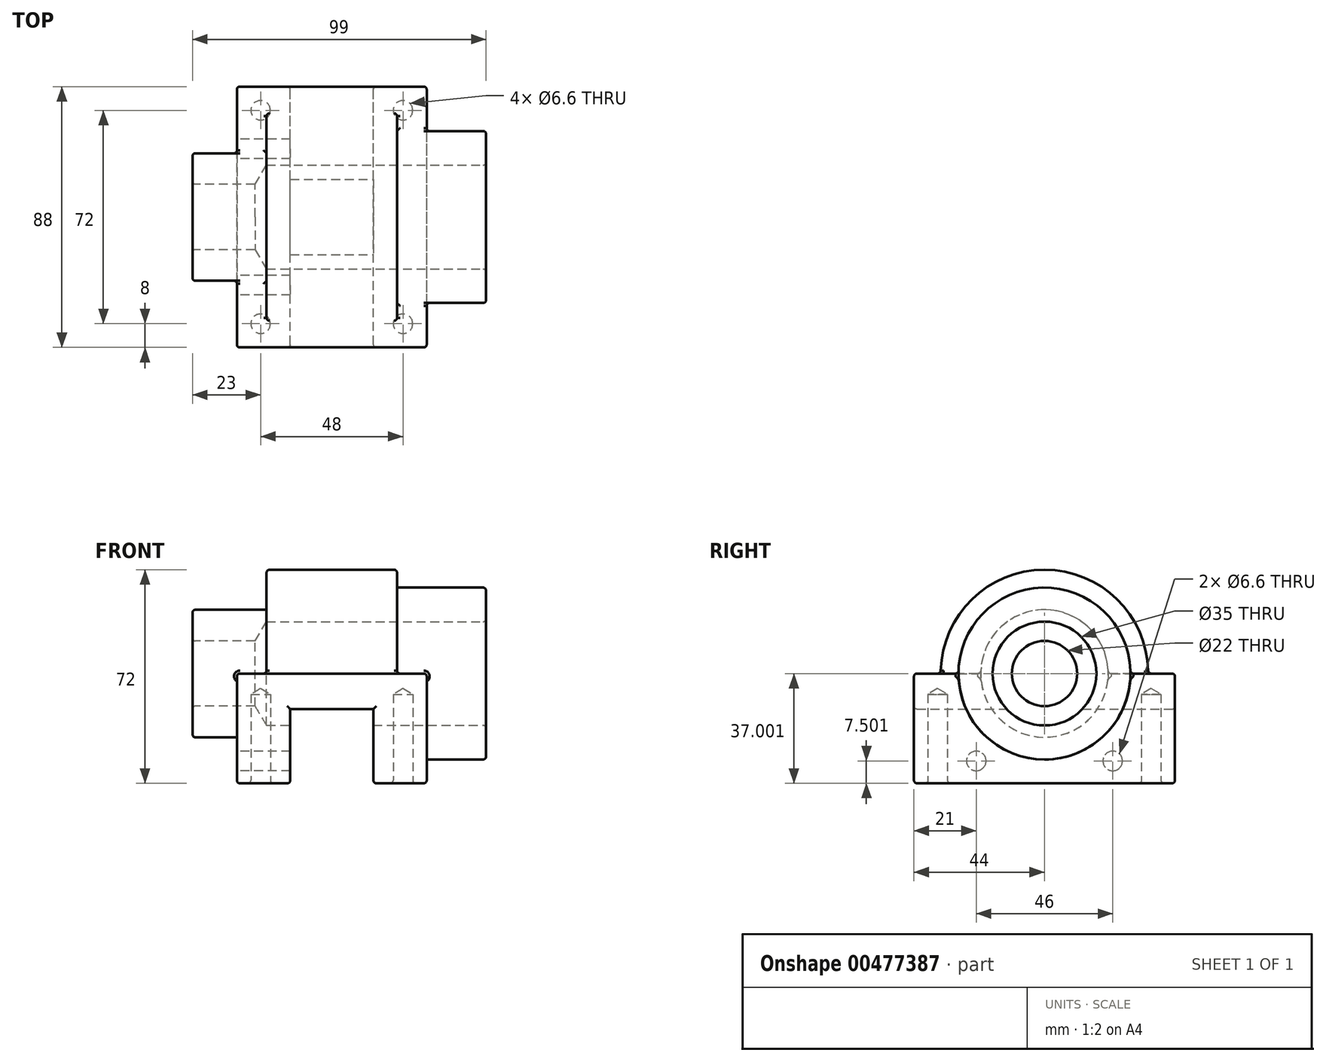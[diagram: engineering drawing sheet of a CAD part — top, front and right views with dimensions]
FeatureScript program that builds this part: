
annotation { "Feature Type Name" : "Feature", "Feature Type Description" : "" }
export const myFeature = defineFeature(function(context is Context, id is Id, definition is map)
    precondition{}
    {
        {
            var Q0;
            Q0=qCreatedBy(makeId("Front.planeOp"),FACE);
            var sketch = newSketch(context, id + "F0", { "sketchPlane" : qUnion([Q0])});
            skLineSegment(sketch, "E0", {"start": v(-32, -20.13) * mm, "end": v(-32, 16.87) * mm});
            skLineSegment(sketch, "E1", {"start": v(-32, 16.87) * mm, "end": v(32, 16.87) * mm});
            skLineSegment(sketch, "E2", {"start": v(32, 16.87) * mm, "end": v(32, -20.13) * mm});
            skLineSegment(sketch, "E3", {"start": v(32, -20.13) * mm, "end": v(14, -20.13) * mm});
            skLineSegment(sketch, "E4", {"start": v(14, -20.13) * mm, "end": v(14, 4.87) * mm});
            skLineSegment(sketch, "E5", {"start": v(14, 4.87) * mm, "end": v(-14, 4.87) * mm});
            skLineSegment(sketch, "E6", {"start": v(-14, 4.87) * mm, "end": v(-14, -20.13) * mm});
            skLineSegment(sketch, "E7", {"start": v(-14, -20.13) * mm, "end": v(-32, -20.13) * mm});
            skSolve(sketch);
        }
        {
            var Q0;
            Q0=makeQuery(id+"F0.imprint","IMPRINT",FACE,{"disambiguationData":[TD([[makeQuery(id+"F0.imprint","IMPRINT",EDGE,{"derivedFrom":sQuery(id+"F0.wireOp",EDGE,"E0")}),-1.0]])]});
            extrude(context, id + "F1", {"entities" : qUnion([Q0]), "depth" : 88 * mm});
        }
        {
            var Q0;
            Q0=makeQuery(id+"F1.opExtrude","SWEPT_FACE",FACE,{"disambiguationData":[OSD([sQuery(id+"F0.wireOp",EDGE,"E2")])]});
            var sketch = newSketch(context, id + "F2", { "sketchPlane" : qUnion([Q0])});
            skCircle(sketch, "E8", {"center": v(-44, 16.87) * mm, "radius": 29 * mm});
            skSolve(sketch);
        }
        {
            var Q0;
            {var subQ0=sQuery(id+"F2.wireOp",EDGE,"E8");var subQ1=makeQuery(id+"F1.opExtrude","SWEPT_EDGE",EDGE,{"disambiguationData":[OSD([sQuery(id+"F0.wireOp",EDGE,"E1"),sQuery(id+"F0.wireOp",EDGE,"E2")])]});var subQ2=makeQuery(id+"F2.imprint","INTERSECT",VERTEX,{"disambiguationData":[OD(0.0)],"derivedFrom":[subQ1,subQ0]});Q0=makeQuery(id+"F2.imprint","IMPRINT",FACE,{"disambiguationData":[TD([[makeQuery(id+"F2.imprint","IMPRINT",EDGE,{"disambiguationData":[TD([[subQ2,1.0]])],"derivedFrom":subQ0}),1.0]])]});}
            var Q1;
            {var subQ0=sQuery(id+"F2.wireOp",EDGE,"E8");var subQ1=makeQuery(id+"F1.opExtrude","SWEPT_EDGE",EDGE,{"disambiguationData":[OSD([sQuery(id+"F0.wireOp",EDGE,"E1"),sQuery(id+"F0.wireOp",EDGE,"E2")])]});var subQ2=makeQuery(id+"F2.imprint","INTERSECT",VERTEX,{"disambiguationData":[OD(0.0)],"derivedFrom":[subQ1,subQ0]});Q1=makeQuery(id+"F2.imprint","IMPRINT",FACE,{"disambiguationData":[TD([[makeQuery(id+"F2.imprint","IMPRINT",EDGE,{"disambiguationData":[TD([[subQ2,-1.0]])],"derivedFrom":subQ0}),1.0]])]});}
            extrude(context, id + "F3", {"entities" : qUnion([Q0, Q1]), "operationType" : NewBodyOperationType.ADD, "depth" : 20 * mm});
        }
        {
            var Q0;
            Q0=makeQuery(id+"F3.opExtrude","CAP_FACE",FACE,{"disambiguationData":[OSD([sQuery(id+"F2.wireOp",EDGE,"E8")])],"isStart":true});
            extrude(context, id + "F4", {"entities" : qUnion([Q0]), "operationType" : NewBodyOperationType.ADD, "depth" : 10 * mm});
        }
        {
            var Q0;
            Q0=makeQuery(id+"F1.opExtrude","SWEPT_FACE",FACE,{"disambiguationData":[OSD([sQuery(id+"F0.wireOp",EDGE,"E0")])]});
            var sketch = newSketch(context, id + "F5", { "sketchPlane" : qUnion([Q0])});
            skCircle(sketch, "E9", {"center": v(44, 16.87) * mm, "radius": 21.5 * mm});
            skSolve(sketch);
        }
        {
            var Q0;
            {var subQ0=sQuery(id+"F5.wireOp",EDGE,"E9");var subQ1=makeQuery(id+"F1.opExtrude","SWEPT_EDGE",EDGE,{"disambiguationData":[OSD([sQuery(id+"F0.wireOp",EDGE,"E0"),sQuery(id+"F0.wireOp",EDGE,"E1")])]});var subQ2=makeQuery(id+"F5.imprint","INTERSECT",VERTEX,{"disambiguationData":[OD(0.0)],"derivedFrom":[subQ1,subQ0]});Q0=makeQuery(id+"F5.imprint","IMPRINT",FACE,{"disambiguationData":[TD([[makeQuery(id+"F5.imprint","IMPRINT",EDGE,{"disambiguationData":[TD([[subQ2,1.0]])],"derivedFrom":subQ0}),1.0]])]});}
            var Q1;
            {var subQ0=sQuery(id+"F5.wireOp",EDGE,"E9");var subQ1=makeQuery(id+"F1.opExtrude","SWEPT_EDGE",EDGE,{"disambiguationData":[OSD([sQuery(id+"F0.wireOp",EDGE,"E0"),sQuery(id+"F0.wireOp",EDGE,"E1")])]});var subQ2=makeQuery(id+"F5.imprint","INTERSECT",VERTEX,{"disambiguationData":[OD(0.0)],"derivedFrom":[subQ1,subQ0]});Q1=makeQuery(id+"F5.imprint","IMPRINT",FACE,{"disambiguationData":[TD([[makeQuery(id+"F5.imprint","IMPRINT",EDGE,{"disambiguationData":[TD([[subQ2,-1.0]])],"derivedFrom":subQ0}),1.0]])]});}
            extrude(context, id + "F6", {"entities" : qUnion([Q0, Q1]), "operationType" : NewBodyOperationType.ADD, "depth" : 15 * mm});
        }
        {
            var Q0;
            Q0=makeQuery(id+"F6.opExtrude","CAP_FACE",FACE,{"disambiguationData":[OSD([sQuery(id+"F5.wireOp",EDGE,"E9")])],"isStart":true});
            extrude(context, id + "F7", {"entities" : qUnion([Q0]), "operationType" : NewBodyOperationType.ADD, "depth" : 10 * mm});
        }
        {
            var Q0;
            Q0=makeQuery(id+"F4.opExtrude","CAP_FACE",FACE,{"disambiguationData":[OSD([sQuery(id+"F2.wireOp",EDGE,"E8")])],"isStart":false});
            var sketch = newSketch(context, id + "F8", { "sketchPlane" : qUnion([Q0])});
            skArc(sketch, "E10", {"start": v(9, 16.87) * mm, "mid": v(44, 51.87) * mm, "end": v(79, 16.87) * mm});
            skLineSegment(sketch, "E11", {"start": v(9, 16.87) * mm, "end": v(79, 16.87) * mm});
            skSolve(sketch);
        }
        {
            var Q0;
            Q0 = qSketchRegion(id + "F8", true);
            extrude(context, id + "F9", {"entities" : qUnion([Q0]), "operationType" : NewBodyOperationType.ADD, "depth" : 44 * mm});
        }
        {
            var Q0;
            Q0=makeQuery(id+"F3.opExtrude","CAP_FACE",FACE,{"disambiguationData":[OSD([sQuery(id+"F2.wireOp",EDGE,"E8")])],"isStart":false});
            var sketch = newSketch(context, id + "F10", { "sketchPlane" : qUnion([Q0])});
            skPoint(sketch, "E12", {"position": v(-44, 16.87) * mm});
            skSolve(sketch);
        }
        {
            var Q0;
            Q0=sQuery(id+"F10.wireOp",VERTEX,"E12");
            var Q1;
            Q1=makeQuery(id+"F1.opExtrude","SWEPT_BODY",BODY,{"disambiguationData":[OSD([sQuery(id+"F0.wireOp",EDGE,"E0"),sQuery(id+"F0.wireOp",EDGE,"E1"),sQuery(id+"F0.wireOp",EDGE,"E2"),sQuery(id+"F0.wireOp",EDGE,"E3"),sQuery(id+"F0.wireOp",EDGE,"E4"),sQuery(id+"F0.wireOp",EDGE,"E5"),sQuery(id+"F0.wireOp",EDGE,"E6"),sQuery(id+"F0.wireOp",EDGE,"E7")])]});
            hole(context, id + "F11", {"style" : HoleStyle.SIMPLE, "endStyle" : HoleEndStyle.BLIND, "holeDiameter" : 35 * mm, "holeDepth" : 74 * mm, "isTappedThrough" : true, "tappedDepth" : 12 * mm, "tapClearance" : 3, "locations" : qUnion([Q0]), "scope" : qUnion([Q1])});
        }
        {
            var Q0;
            Q0=makeQuery(id+"F6.opExtrude","CAP_FACE",FACE,{"disambiguationData":[OSD([sQuery(id+"F5.wireOp",EDGE,"E9")])],"isStart":false});
            var sketch = newSketch(context, id + "F12", { "sketchPlane" : qUnion([Q0])});
            skPoint(sketch, "E13", {"position": v(44, 16.87) * mm});
            skSolve(sketch);
        }
        {
            var Q0;
            Q0=sQuery(id+"F12.wireOp",VERTEX,"E13");
            var Q1;
            Q1=makeQuery(id+"F1.opExtrude","SWEPT_BODY",BODY,{"disambiguationData":[OSD([sQuery(id+"F0.wireOp",EDGE,"E0"),sQuery(id+"F0.wireOp",EDGE,"E1"),sQuery(id+"F0.wireOp",EDGE,"E2"),sQuery(id+"F0.wireOp",EDGE,"E3"),sQuery(id+"F0.wireOp",EDGE,"E4"),sQuery(id+"F0.wireOp",EDGE,"E5"),sQuery(id+"F0.wireOp",EDGE,"E6"),sQuery(id+"F0.wireOp",EDGE,"E7")])]});
            hole(context, id + "F13", {"style" : HoleStyle.SIMPLE, "endStyle" : HoleEndStyle.BLIND, "holeDiameter" : 22 * mm, "holeDepth" : 25 * mm, "isTappedThrough" : true, "tappedDepth" : 12 * mm, "tapClearance" : 3, "locations" : qUnion([Q0]), "scope" : qUnion([Q1])});
        }
        {
            var Q0;
            Q0=makeQuery(id+"F1.opExtrude","SWEPT_FACE",FACE,{"disambiguationData":[OSD([sQuery(id+"F0.wireOp",EDGE,"E7")])]});
            var sketch = newSketch(context, id + "F14", { "sketchPlane" : qUnion([Q0])});
            skPoint(sketch, "E14", {"position": v(-24, 80) * mm});
            skPoint(sketch, "E15", {"position": v(-24, 8) * mm});
            skPoint(sketch, "E16.MirrorP", {"position": v(24, 8) * mm});
            skPoint(sketch, "E17.MirrorP", {"position": v(24, 80) * mm});
            skSolve(sketch);
        }
        {
            var Q0;
            Q0=sQuery(id+"F14.wireOp",VERTEX,"E14");
            var Q1;
            Q1=sQuery(id+"F14.wireOp",VERTEX,"E17.MirrorP");
            var Q2;
            Q2=sQuery(id+"F14.wireOp",VERTEX,"E15");
            var Q3;
            Q3=sQuery(id+"F14.wireOp",VERTEX,"E16.MirrorP");
            var Q4;
            Q4=makeQuery(id+"F1.opExtrude","SWEPT_BODY",BODY,{"disambiguationData":[OSD([sQuery(id+"F0.wireOp",EDGE,"E0"),sQuery(id+"F0.wireOp",EDGE,"E1"),sQuery(id+"F0.wireOp",EDGE,"E2"),sQuery(id+"F0.wireOp",EDGE,"E3"),sQuery(id+"F0.wireOp",EDGE,"E4"),sQuery(id+"F0.wireOp",EDGE,"E5"),sQuery(id+"F0.wireOp",EDGE,"E6"),sQuery(id+"F0.wireOp",EDGE,"E7")])]});
            hole(context, id + "F15", {"style" : HoleStyle.SIMPLE, "endStyle" : HoleEndStyle.BLIND, "standardTappedOrClearance" : lookupTablePath({ "standard" : "ISO", "fit" : "Normal", "size" : "M6", "type" : "Clearance" }), "standardBlindInLast" : lookupTablePath({ "fit" : "Standard", "standard" : "ISO", "size" : "M6", "type" : "Clearance" }), "holeDiameter" : 6.6 * mm, "holeDepth" : 30 * mm, "isTappedThrough" : true, "tappedDepth" : 12 * mm, "tapClearance" : 3, "locations" : qUnion([Q0, Q1, Q2, Q3]), "scope" : qUnion([Q4])});
        }
        {
            var Q0;
            Q0=makeQuery(id+"F1.opExtrude","SWEPT_FACE",FACE,{"disambiguationData":[OSD([sQuery(id+"F0.wireOp",EDGE,"E0")])]});
            var sketch = newSketch(context, id + "F16", { "sketchPlane" : qUnion([Q0])});
            skPoint(sketch, "E18", {"position": v(67, -12.63) * mm});
            skPoint(sketch, "E19", {"position": v(21, -12.63) * mm});
            skSolve(sketch);
        }
        {
            var Q0;
            Q0=sQuery(id+"F16.wireOp",VERTEX,"E18");
            var Q1;
            Q1=sQuery(id+"F16.wireOp",VERTEX,"E19");
            var Q2;
            Q2=makeQuery(id+"F1.opExtrude","SWEPT_BODY",BODY,{"disambiguationData":[OSD([sQuery(id+"F0.wireOp",EDGE,"E0"),sQuery(id+"F0.wireOp",EDGE,"E1"),sQuery(id+"F0.wireOp",EDGE,"E2"),sQuery(id+"F0.wireOp",EDGE,"E3"),sQuery(id+"F0.wireOp",EDGE,"E4"),sQuery(id+"F0.wireOp",EDGE,"E5"),sQuery(id+"F0.wireOp",EDGE,"E6"),sQuery(id+"F0.wireOp",EDGE,"E7")])]});
            hole(context, id + "F17", {"style" : HoleStyle.SIMPLE, "endStyle" : HoleEndStyle.BLIND, "standardTappedOrClearance" : lookupTablePath({ "standard" : "ISO", "fit" : "Normal", "size" : "M6", "type" : "Clearance" }), "standardBlindInLast" : lookupTablePath({ "fit" : "Standard", "standard" : "ISO", "size" : "M6", "type" : "Clearance" }), "holeDiameter" : 6.6 * mm, "holeDepth" : 30 * mm, "isTappedThrough" : true, "tappedDepth" : 12 * mm, "tapClearance" : 3, "locations" : qUnion([Q0, Q1]), "scope" : qUnion([Q2])});
        }
        {
            var Q0;
            Q0=makeQuery(id+"F1.opExtrude","SWEPT_FACE",FACE,{"disambiguationData":[OSD([sQuery(id+"F0.wireOp",EDGE,"E7")])]});
            var Q1;
            Q1=makeQuery(id+"F1.opExtrude","SWEPT_FACE",FACE,{"disambiguationData":[OSD([sQuery(id+"F0.wireOp",EDGE,"E3")])]});
            var Q2;
            Q2=makeQuery(id+"F1.opExtrude","CAP_FACE",FACE,{"disambiguationData":[OSD([sQuery(id+"F0.wireOp",EDGE,"E0"),sQuery(id+"F0.wireOp",EDGE,"E1"),sQuery(id+"F0.wireOp",EDGE,"E2"),sQuery(id+"F0.wireOp",EDGE,"E3"),sQuery(id+"F0.wireOp",EDGE,"E4"),sQuery(id+"F0.wireOp",EDGE,"E5"),sQuery(id+"F0.wireOp",EDGE,"E6"),sQuery(id+"F0.wireOp",EDGE,"E7")])],"isStart":false});
            var Q3;
            Q3=makeQuery(id+"F1.opExtrude","CAP_FACE",FACE,{"disambiguationData":[OSD([sQuery(id+"F0.wireOp",EDGE,"E0"),sQuery(id+"F0.wireOp",EDGE,"E1"),sQuery(id+"F0.wireOp",EDGE,"E2"),sQuery(id+"F0.wireOp",EDGE,"E3"),sQuery(id+"F0.wireOp",EDGE,"E4"),sQuery(id+"F0.wireOp",EDGE,"E5"),sQuery(id+"F0.wireOp",EDGE,"E6"),sQuery(id+"F0.wireOp",EDGE,"E7")])],"isStart":true});
            var Q4;
            {var subQ1=sQuery(id+"F0.wireOp",EDGE,"E2");var subQ2=sQuery(id+"F0.wireOp",EDGE,"E1");var subQ3=sQuery(id+"F0.wireOp",EDGE,"E0");Q4=makeQuery(id+"F9.boolean.opBoolean","SPLIT",FACE,{"disambiguationData":[TD([makeQuery(id+"F1.opExtrude","CAP_FACE",FACE,{"disambiguationData":[OSD([subQ3,subQ2,subQ1,sQuery(id+"F0.wireOp",EDGE,"E3"),sQuery(id+"F0.wireOp",EDGE,"E4"),sQuery(id+"F0.wireOp",EDGE,"E5"),sQuery(id+"F0.wireOp",EDGE,"E6"),sQuery(id+"F0.wireOp",EDGE,"E7")])],"isStart":true})])],"derivedFrom":makeQuery(id+"F1.opExtrude","SWEPT_FACE",FACE,{"disambiguationData":[OSD([subQ2])]})});}
            var Q5;
            {var subQ2=sQuery(id+"F0.wireOp",EDGE,"E2");var subQ3=sQuery(id+"F0.wireOp",EDGE,"E1");var subQ4=sQuery(id+"F0.wireOp",EDGE,"E0");Q5=makeQuery(id+"F9.boolean.opBoolean","SPLIT",FACE,{"disambiguationData":[TD([makeQuery(id+"F1.opExtrude","CAP_FACE",FACE,{"disambiguationData":[OSD([subQ4,subQ3,subQ2,sQuery(id+"F0.wireOp",EDGE,"E3"),sQuery(id+"F0.wireOp",EDGE,"E4"),sQuery(id+"F0.wireOp",EDGE,"E5"),sQuery(id+"F0.wireOp",EDGE,"E6"),sQuery(id+"F0.wireOp",EDGE,"E7")])],"isStart":false})])],"derivedFrom":makeQuery(id+"F1.opExtrude","SWEPT_FACE",FACE,{"disambiguationData":[OSD([subQ3])]})});}
            var Q6;
            Q6=makeQuery(id+"F3.opExtrude","CAP_FACE",FACE,{"disambiguationData":[OSD([sQuery(id+"F2.wireOp",EDGE,"E8")])],"isStart":false});
            var Q7;
            Q7=makeQuery(id+"F6.opExtrude","CAP_FACE",FACE,{"disambiguationData":[OSD([sQuery(id+"F5.wireOp",EDGE,"E9")])],"isStart":false});
            var Q8;
            Q8=makeQuery(id+"F17.hole-0.boolean.opBoolean","COPY",EDGE,{"derivedFrom":makeQuery(id+"F17.hole-0.opRevolve","SWEPT_EDGE",EDGE,{"disambiguationData":[OSD([sQuery(id+"F17.hole-0.sketch.wireOp",EDGE,"core_line_2"),sQuery(id+"F17.hole-0.sketch.wireOp",EDGE,"core_line_3")])]})});
            var Q9;
            Q9=makeQuery(id+"F17.hole-1.boolean.opBoolean","COPY",EDGE,{"derivedFrom":makeQuery(id+"F17.hole-1.opRevolve","SWEPT_EDGE",EDGE,{"disambiguationData":[OSD([sQuery(id+"F17.hole-1.sketch.wireOp",EDGE,"core_line_2"),sQuery(id+"F17.hole-1.sketch.wireOp",EDGE,"core_line_3")])]})});
            var Q10;
            Q10=makeQuery(id+"F9.opExtrude","SWEPT_FACE",FACE,{"disambiguationData":[OSD([sQuery(id+"F8.wireOp",EDGE,"E10")])]});
            fillet(context, id + "F18", {"entities" : qUnion([Q0, Q1, Q2, Q3, Q4, Q5, Q6, Q7, Q8, Q9, Q10]), "radius" : 1 * mm, "tangentPropagation" : true, "allowEdgeOverflow" : false});
        }
    });
